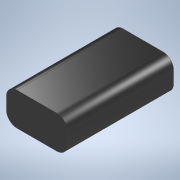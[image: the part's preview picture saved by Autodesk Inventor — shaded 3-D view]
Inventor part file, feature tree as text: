
AUTODESK INVENTOR PART (.ipt)
format: ipt  version: 2021 (Build 250183000, 183)  size: 108,544 bytes
history: native  units: mm
features: extrude x1, fillet x1, sketch x1
ambient origin geometry x8: Origin, YZ Plane, XZ Plane, XY Plane, X Axis, Y Axis, Z Axis, Center Point
bodies: Solid1 (feature_tree)
feature tree (3):
  extrude  "Extrusion1"  Depth=6.2mm
  fillet  "Fillet1"  Radius=20.0mm
  sketch  "Sketch1"  dims[d0=11.5mm d1=6.2mm d2=20.0mm d3=0.0mm d4=2.0mm]
